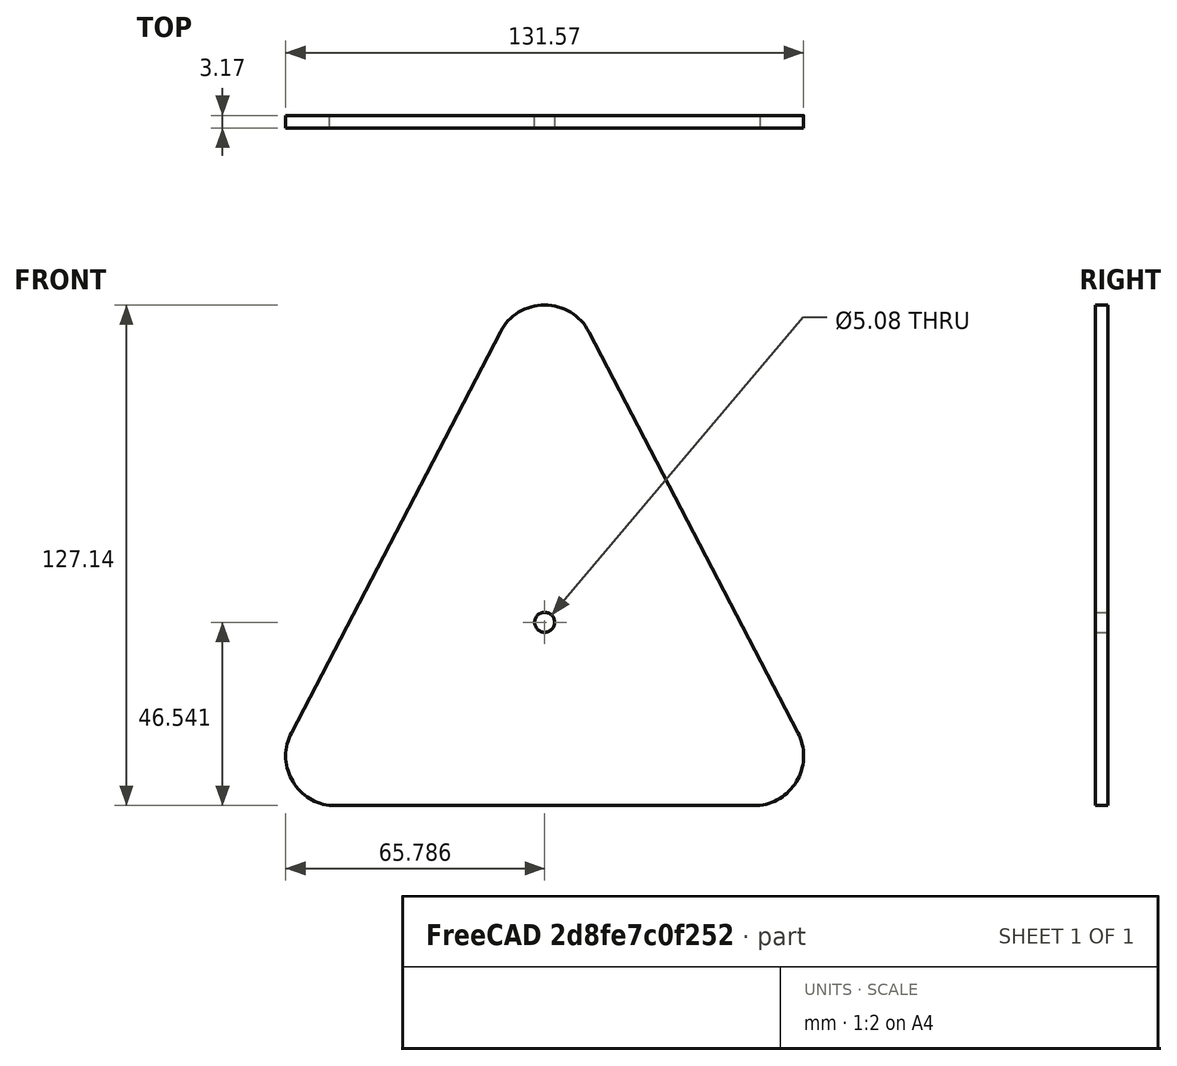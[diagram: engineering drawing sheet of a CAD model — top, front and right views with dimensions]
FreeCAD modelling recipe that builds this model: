
FCSTD DOCUMENT  (FreeCAD 0.19R24291 (Git))
Label: floating_point_triangle
License: All rights reserved
LicenseURL: http://en.wikipedia.org/wiki/All_rights_reserved
objects: PartDesign::Body×2, Sketcher::SketchObject×1, Part::Extrusion×1
note: 4 computed .brp shape members not serialized (recipe doc carries the construction recipe); baked Part::Feature solids carry a one-line shape summary decoded from their .brp

FEATURE [PartDesign::Body] Body
  Origin = -> Origin
FEATURE [Sketcher::SketchObject] Sketch
  FullyConstrained = true
  MapMode = 5
  Placement = pos=(0,0,0) rot=(1,0,0;1.5708rad)
  Support = -> [XZ_Plane001]
  sketch-geometry (20):
    g0: LineSegment StartX=0 StartY=0 StartZ=0 EndX=106.172 EndY=0 EndZ=0
    g1: LineSegment StartX=53.086 StartY=101.854 StartZ=0 EndX=106.172 EndY=0 EndZ=0
    g2: LineSegment StartX=53.086 StartY=101.854 StartZ=0 EndX=0 EndY=0 EndZ=0
    g3: GeomPoint X=53.086 Y=0 Z=0
    g4: LineSegment StartX=53.086 StartY=101.854 StartZ=0 EndX=53.086 EndY=0 EndZ=0
    g5: ArcOfCircle CenterX=106.172 CenterY=0 CenterZ=0 NormalX=0 NormalY=0 NormalZ=1 AngleXU=0 Radius=12.7 StartAngle=4.8418 EndAngle=6.76365
    g6: ArcOfCircle CenterX=0 CenterY=0 CenterZ=0 NormalX=0 NormalY=0 NormalZ=1 AngleXU=0 Radius=12.7 StartAngle=2.66113 EndAngle=4.58298
    g7: LineSegment StartX=-11.2621 StartY=5.86979 StartZ=0 EndX=41.8239 EndY=107.724 EndZ=0
    g8: LineSegment StartX=64.3481 StartY=107.724 StartZ=0 EndX=117.434 EndY=5.86981 EndZ=0
    g9: GeomPoint X=79.629 Y=50.927 Z=0
    g10: Circle CenterX=106.172 CenterY=0 CenterZ=0 NormalX=0 NormalY=0 NormalZ=1 AngleXU=0 Radius=57.429
    g11: Circle CenterX=53.086 CenterY=101.854 CenterZ=0 NormalX=0 NormalY=0 NormalZ=1 AngleXU=0 Radius=57.429
    g12: LineSegment StartX=79.629 StartY=50.927 StartZ=0 EndX=0 EndY=0 EndZ=0
    g13: GeomPoint X=53.086 Y=33.9513 Z=0
    g14: LineSegment StartX=-1.63896 StartY=-12.5938 StartZ=0 EndX=107.811 EndY=-12.5938 EndZ=0
    g15: ArcOfCircle CenterX=53.086 CenterY=101.854 CenterZ=0 NormalX=0 NormalY=0 NormalZ=1 AngleXU=0 Radius=12.7 StartAngle=0.480461 EndAngle=2.66113
    g16: LineSegment StartX=41.8239 StartY=107.724 StartZ=0 EndX=64.3481 EndY=107.724 EndZ=0
    g17: LineSegment StartX=-11.2621 StartY=5.86979 StartZ=0 EndX=-1.63896 EndY=-12.5938 EndZ=0
    g18: LineSegment StartX=117.434 StartY=5.86981 StartZ=0 EndX=107.811 EndY=-12.5938 EndZ=0
    g19: Circle CenterX=53.086 CenterY=33.9513 CenterZ=0 NormalX=0 NormalY=0 NormalZ=1 AngleXU=0 Radius=2.54
  constraints (48):
    c: Coincident(g0,g-1)
    c: PointOnObject(g0,g-1)
    c: Coincident(g1,g0)
    c: Coincident(g2,g1)
    c: Coincident(g2,g0)
    c: Distance(g0) = 106.172
    c: Distance(g1,g0) = 101.854
    c: PointOnObject(g3,g0)
    c: Coincident(g4,g1)
    c: Coincident(g4,g3)
    c: Vertical(g4)
    c: Distance(g0,g4) = 53.086
    c: Coincident(g5,g0)
    c: Radius(g5) = 12.7
    c: Coincident(g6,g0)
    c: Radius(g6) = 12.7
    c: Parallel(g2,g7)
    c: Parallel(g1,g8)
    c: PointOnObject(g9,g1)
    c: Coincident(g10,g0)
    c: PointOnObject(g9,g10)
    c: Coincident(g11,g1)
    c: PointOnObject(g9,g11)
    c: Equal(g11,g10)
    c: Coincident(g12,g9)
    c: Coincident(g12,g0)
    c: PointOnObject(g13,g4)
    c: PointOnObject(g13,g12)
    c: Coincident(g15,g7) = 1.5708
    c: Tangent(g15,g8) = 1.5708
    c: Coincident(g6,g7)
    c: Coincident(g5,g14)
    c: Coincident(g5,g8)
    c: Coincident(g6,g14)
    c: Coincident(g16,g7)
    c: Coincident(g16,g8)
    c: Parallel(g16,g14)
    c: Coincident(g17,g6)
    c: Coincident(g17,g6)
    c: Parallel(g17,g8)
    c: Coincident(g18,g5)
    c: Coincident(g18,g5)
    c: Parallel(g7,g18)
    c: Tangent(g7,g6)
    c: Radius(g15) = 12.7
    c: Tangent(g8,g5)
    c: Coincident(g19,g13)
    c: Radius(g19) = 2.54
FEATURE [PartDesign::Body] Body001
  Group = -> [Sketch]
  Origin = -> Origin001
FEATURE [Part::Extrusion] Extrude
  Base = -> Sketch
  Dir = (0,-1,-2e-16)
  DirMode = 2
  FaceMakerClass = Part::FaceMakerBullseye
  LengthFwd = 3.175
  LengthRev = 0
  Solid = true
  Symmetric = false
